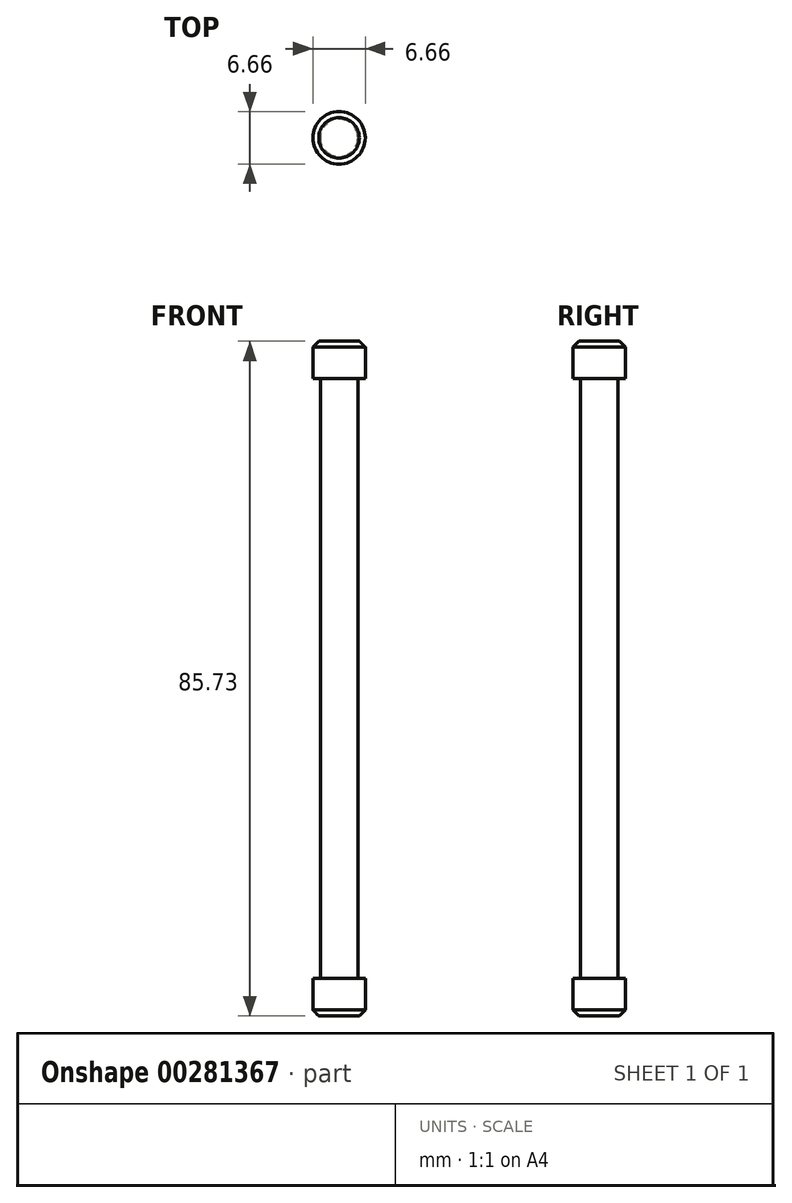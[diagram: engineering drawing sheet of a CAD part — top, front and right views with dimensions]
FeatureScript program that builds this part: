
annotation { "Feature Type Name" : "Feature", "Feature Type Description" : "" }
export const myFeature = defineFeature(function(context is Context, id is Id, definition is map)
    precondition{}
    {
        {
            var Q0;
            Q0=qCreatedBy(makeId("Top.planeOp"),FACE);
            var sketch = newSketch(context, id + "F0", { "sketchPlane" : qUnion([Q0])});
            skCircle(sketch, "E0", {"center": v(0, 0) * mm, "radius": 3.33 * mm});
            skSolve(sketch);
        }
        {
            var Q0;
            Q0 = qSketchRegion(id + "F0", true);
            extrude(context, id + "F1", {"entities" : qUnion([Q0]), "oppositeDirection" : true, "depth" : 4.76 * mm});
        }
        {
            var Q0;
            Q0=makeQuery(id+"F1.opExtrude","CAP_FACE",FACE,{"disambiguationData":[OSD([sQuery(id+"F0.wireOp",EDGE,"E0")])],"isStart":false});
            var sketch = newSketch(context, id + "F2", { "sketchPlane" : qUnion([Q0])});
            skCircle(sketch, "E1", {"center": v(0, 0) * mm, "radius": 2.38 * mm});
            skSolve(sketch);
        }
        {
            var Q0;
            Q0 = qSketchRegion(id + "F2", true);
            extrude(context, id + "F3", {"entities" : qUnion([Q0]), "operationType" : NewBodyOperationType.ADD, "depth" : 76.2 * mm});
        }
        {
            var Q0;
            Q0=makeQuery(id+"F3.opExtrude","CAP_FACE",FACE,{"disambiguationData":[OSD([sQuery(id+"F2.wireOp",EDGE,"E1")])],"isStart":false});
            var sketch = newSketch(context, id + "F4", { "sketchPlane" : qUnion([Q0])});
            skCircle(sketch, "E2", {"center": v(0, 0) * mm, "radius": 3.33 * mm});
            skSolve(sketch);
        }
        {
            var Q0;
            Q0 = qSketchRegion(id + "F4", true);
            extrude(context, id + "F5", {"entities" : qUnion([Q0]), "operationType" : NewBodyOperationType.ADD, "depth" : 4.76 * mm});
        }
        {
            var Q0;
            Q0=makeQuery(id+"F1.opExtrude","CAP_EDGE",EDGE,{"disambiguationData":[OSD([sQuery(id+"F0.wireOp",EDGE,"E0")])],"isStart":true});
            var Q1;
            Q1=makeQuery(id+"F5.opExtrude","CAP_EDGE",EDGE,{"disambiguationData":[OSD([sQuery(id+"F4.wireOp",EDGE,"E2")])],"isStart":false});
            chamfer(context, id + "F6", {"entities" : qUnion([Q0, Q1]), "width" : 0.76 * mm, "tangentPropagation" : true});
        }
    });
